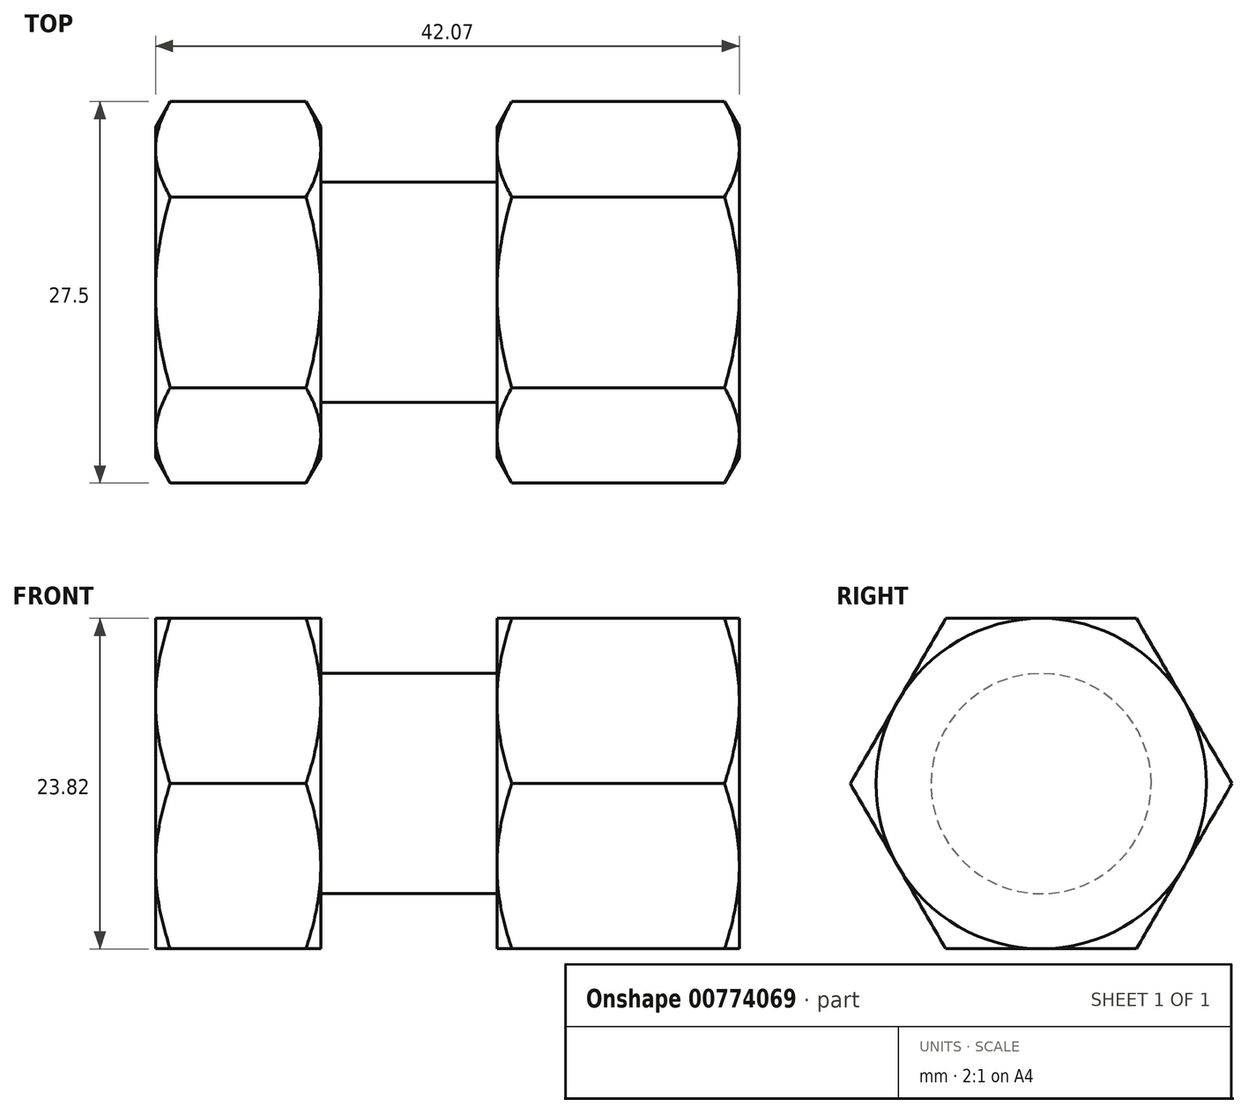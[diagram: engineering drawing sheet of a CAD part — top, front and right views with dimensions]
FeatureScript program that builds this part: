
annotation { "Feature Type Name" : "Feature", "Feature Type Description" : "" }
export const myFeature = defineFeature(function(context is Context, id is Id, definition is map)
    precondition{}
    {
        {
            var Q0;
            Q0=qCreatedBy(makeId("Front.planeOp"),FACE);
            var sketch = newSketch(context, id + "F0", { "sketchPlane" : qUnion([Q0])});
            skLineSegment(sketch, "E0", {"start": v(0, 0) * mm, "end": v(25.4, 0) * mm});
            skLineSegment(sketch, "E1", {"start": v(0, 0) * mm, "end": v(0, 7.94) * mm});
            skLineSegment(sketch, "E2", {"start": v(0, 7.94) * mm, "end": v(25.4, 7.94) * mm});
            skLineSegment(sketch, "E3", {"start": v(25.4, 7.94) * mm, "end": v(25.4, 0) * mm});
            skSolve(sketch);
        }
        {
            var Q0;
            Q0=makeQuery(id+"F0.imprint","IMPRINT",FACE,{"disambiguationData":[TD([[makeQuery(id+"F0.imprint","IMPRINT",EDGE,{"derivedFrom":sQuery(id+"F0.wireOp",EDGE,"E0")}),1.0]])]});
            var Q1;
            Q1=sQuery(id+"F0.wireOp",EDGE,"E0");
            revolve(context, id + "F1", {"surfaceOperationType" : NewSurfaceOperationType.NEW, "entities" : qUnion([Q0]), "axis" : qUnion([Q1]), "revolveType" : RevolveType.FULL});
        }
        {
            var Q0;
            Q0=qCreatedBy(makeId("Right.planeOp"),FACE);
            var sketch = newSketch(context, id + "F2", { "sketchPlane" : qUnion([Q0])});
            skCircle(sketch, "E4.cCircle", {"center": v(0, 0) * mm, "radius": 11.9 * mm, "construction": true});
            skLineSegment(sketch, "E4.0", {"start": v(-6.87, 11.9) * mm, "end": v(6.87, 11.9) * mm});
            skLineSegment(sketch, "E4.1", {"start": v(6.87, 11.9) * mm, "end": v(13.75, 0) * mm});
            skLineSegment(sketch, "E4.2", {"start": v(13.75, 0) * mm, "end": v(6.87, -11.9) * mm});
            skLineSegment(sketch, "E4.3", {"start": v(6.87, -11.9) * mm, "end": v(-6.87, -11.9) * mm});
            skLineSegment(sketch, "E4.4", {"start": v(-6.87, -11.9) * mm, "end": v(-13.75, 0) * mm});
            skLineSegment(sketch, "E4.5", {"start": v(-13.75, 0) * mm, "end": v(-6.87, 11.9) * mm});
            skPoint(sketch, "E4.0.midPoint", {"position": v(0, 11.9) * mm});
            skSolve(sketch);
        }
        {
            var Q0;
            Q0 = qSketchRegion(id + "F2", true);
            extrude(context, id + "F3", {"entities" : qUnion([Q0]), "operationType" : NewBodyOperationType.ADD, "depth" : 11.9 * mm, "offsetDistance" : 25.4 * mm});
        }
        {
            var Q0;
            Q0=makeQuery(id+"F3.opExtrude","CAP_FACE",FACE,{"disambiguationData":[OSD([sQuery(id+"F2.wireOp",EDGE,"E4.0"),sQuery(id+"F2.wireOp",EDGE,"E4.1"),sQuery(id+"F2.wireOp",EDGE,"E4.2"),sQuery(id+"F2.wireOp",EDGE,"E4.3"),sQuery(id+"F2.wireOp",EDGE,"E4.4"),sQuery(id+"F2.wireOp",EDGE,"E4.5")])],"isStart":false});
            cPlane(context, id + "F4", {"entities" : qUnion([Q0]), "cplaneType" : CPlaneType.OFFSET, "offset" : 12.7 * mm, "width" : 152.4 * mm, "height" : 152.4 * mm});
        }
        {
            var Q0;
            Q0=qCreatedBy(id+"F4.planeOp",FACE);
            var sketch = newSketch(context, id + "F5", { "sketchPlane" : qUnion([Q0])});
            skCircle(sketch, "E5.cCircle", {"center": v(0, 0) * mm, "radius": 11.9 * mm, "construction": true});
            skLineSegment(sketch, "E5.0", {"start": v(13.75, 0) * mm, "end": v(6.87, -11.9) * mm});
            skLineSegment(sketch, "E5.1", {"start": v(6.87, -11.9) * mm, "end": v(-6.87, -11.9) * mm});
            skLineSegment(sketch, "E5.2", {"start": v(-6.87, -11.9) * mm, "end": v(-13.75, 0) * mm});
            skLineSegment(sketch, "E5.3", {"start": v(-13.75, 0) * mm, "end": v(-6.87, 11.9) * mm});
            skLineSegment(sketch, "E5.4", {"start": v(-6.87, 11.9) * mm, "end": v(6.87, 11.9) * mm});
            skLineSegment(sketch, "E5.5", {"start": v(6.87, 11.9) * mm, "end": v(13.75, 0) * mm});
            skPoint(sketch, "E5.0.midPoint", {"position": v(10.31, -5.95) * mm});
            skSolve(sketch);
        }
        {
            var Q0;
            Q0 = qSketchRegion(id + "F5", true);
            extrude(context, id + "F6", {"entities" : qUnion([Q0]), "operationType" : NewBodyOperationType.ADD, "depth" : 17.46 * mm, "offsetDistance" : 25.4 * mm});
        }
        {
            var Q0;
            Q0=qCreatedBy(makeId("Front.planeOp"),FACE);
            var sketch = newSketch(context, id + "F7", { "sketchPlane" : qUnion([Q0])});
            skLineSegment(sketch, "E6", {"start": v(0, 0) * mm, "end": v(78.79, 0) * mm, "construction": true});
            skLineSegment(sketch, "E7", {"start": v(0, 11.9) * mm, "end": v(3.95, 18.75) * mm});
            skLineSegment(sketch, "E8", {"start": v(3.95, 18.75) * mm, "end": v(0, 18.75) * mm});
            skLineSegment(sketch, "E9", {"start": v(0, 18.75) * mm, "end": v(0, 11.9) * mm});
            skLineSegment(sketch, "E10", {"start": v(11.9, 11.9) * mm, "end": v(11.9, 18.75) * mm});
            skLineSegment(sketch, "E11", {"start": v(11.9, 18.75) * mm, "end": v(7.95, 18.75) * mm});
            skLineSegment(sketch, "E12", {"start": v(7.95, 18.75) * mm, "end": v(11.9, 11.9) * mm});
            skLineSegment(sketch, "E13", {"start": v(24.6, 11.9) * mm, "end": v(24.6, 18.75) * mm});
            skLineSegment(sketch, "E14", {"start": v(24.6, 18.75) * mm, "end": v(28.56, 18.75) * mm});
            skLineSegment(sketch, "E15", {"start": v(28.56, 18.75) * mm, "end": v(24.6, 11.9) * mm});
            skLineSegment(sketch, "E16", {"start": v(42.07, 18.75) * mm, "end": v(42.07, 11.9) * mm});
            skLineSegment(sketch, "E17", {"start": v(42.07, 11.9) * mm, "end": v(38.12, 18.75) * mm});
            skLineSegment(sketch, "E18", {"start": v(38.12, 18.75) * mm, "end": v(42.07, 18.75) * mm});
            skSolve(sketch);
        }
        {
            var Q0;
            Q0 = qSketchRegion(id + "F7", true);
            var Q1;
            Q1=sQuery(id+"F7.wireOp",EDGE,"E6");
            revolve(context, id + "F8", {"operationType" : NewBodyOperationType.REMOVE, "surfaceOperationType" : NewSurfaceOperationType.NEW, "entities" : qUnion([Q0]), "axis" : qUnion([Q1]), "revolveType" : RevolveType.FULL});
        }
    });
